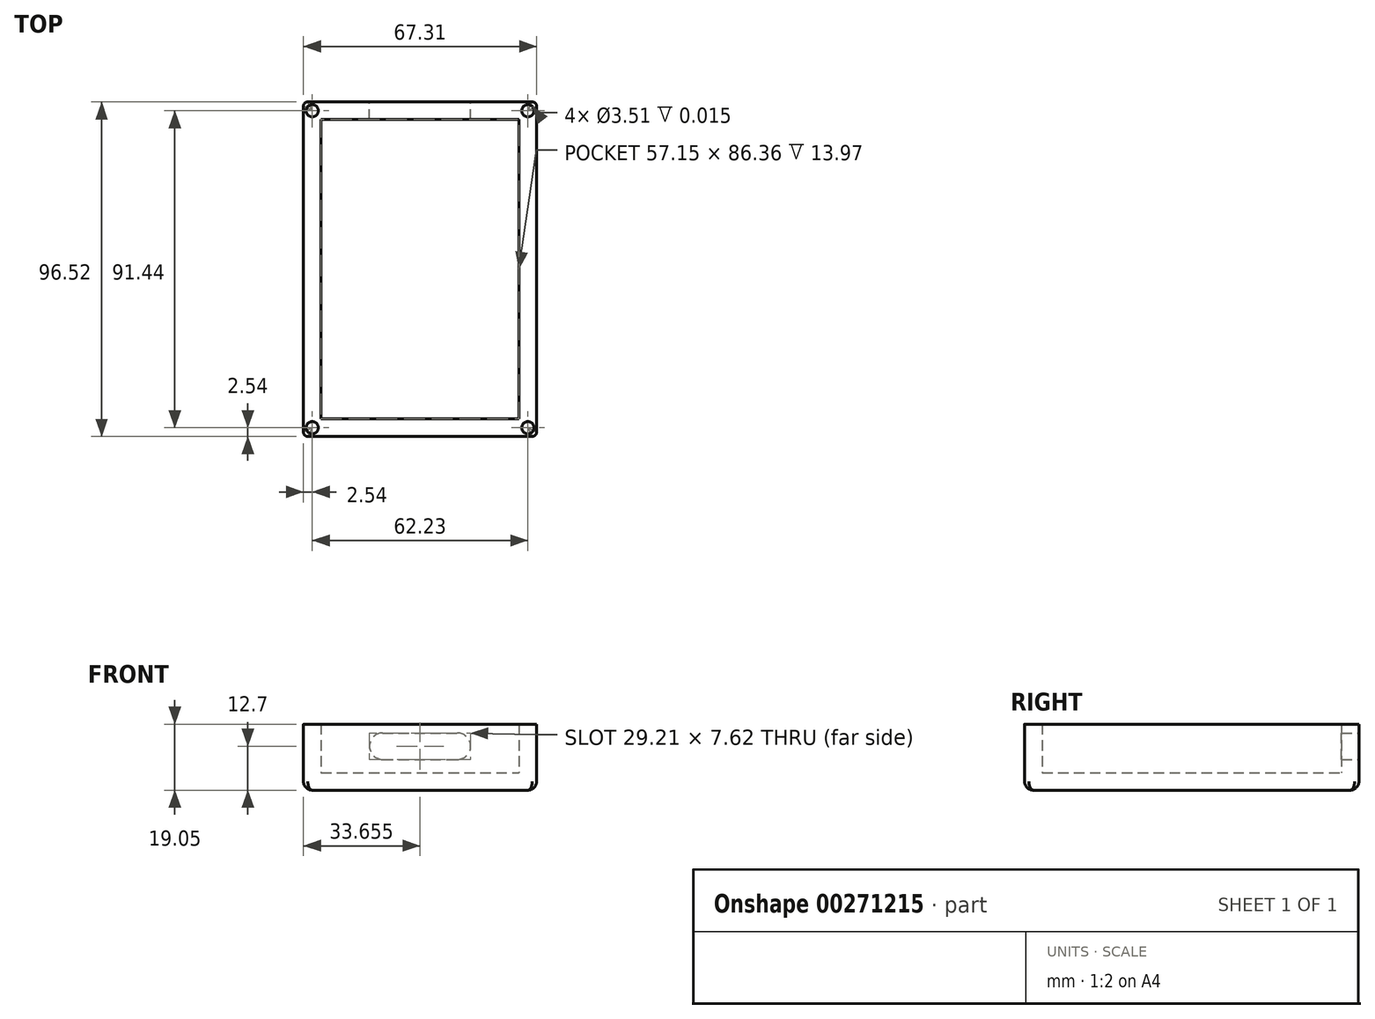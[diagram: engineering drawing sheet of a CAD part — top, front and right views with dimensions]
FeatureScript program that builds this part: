
annotation { "Feature Type Name" : "Feature", "Feature Type Description" : "" }
export const myFeature = defineFeature(function(context is Context, id is Id, definition is map)
    precondition{}
    {
        {
            var Q0;
            Q0=qCreatedBy(makeId("Top.planeOp"),FACE);
            var sketch = newSketch(context, id + "F0", { "sketchPlane" : qUnion([Q0])});
            skLineSegment(sketch, "E0.bottom", {"start": v(1.27, 0) * mm, "end": v(66.04, 0) * mm});
            skLineSegment(sketch, "E0.top", {"start": v(1.27, 96.52) * mm, "end": v(66.04, 96.52) * mm});
            skLineSegment(sketch, "E0.left", {"start": v(0, 1.27) * mm, "end": v(0, 95.25) * mm});
            skLineSegment(sketch, "E0.right", {"start": v(67.31, 1.27) * mm, "end": v(67.3, 95.25) * mm});
            skPoint(sketch, "E1.visualSharp", {"position": v(0, 96.52) * mm});
            skArc(sketch, "E1.filletArc", {"start": v(1.27, 96.52) * mm, "mid": v(0.37, 96.15) * mm, "end": v(0, 95.25) * mm});
            skPoint(sketch, "E2.visualSharp", {"position": v(67.3, 96.52) * mm});
            skArc(sketch, "E2.filletArc", {"start": v(67.31, 95.25) * mm, "mid": v(66.94, 96.15) * mm, "end": v(66.04, 96.52) * mm});
            skPoint(sketch, "E3.visualSharp", {"position": v(67.31, 0) * mm});
            skArc(sketch, "E3.filletArc", {"start": v(66.04, 0) * mm, "mid": v(66.94, 0.37) * mm, "end": v(67.31, 1.27) * mm});
            skPoint(sketch, "E4.visualSharp", {"position": v(0, 0) * mm});
            skArc(sketch, "E4.filletArc", {"start": v(0, 1.27) * mm, "mid": v(0.37, 0.37) * mm, "end": v(1.27, 0) * mm});
            skSolve(sketch);
        }
        {
            var Q0;
            Q0 = qSketchRegion(id + "F0", true);
            extrude(context, id + "F1", {"entities" : qUnion([Q0]), "depth" : 19.05 * mm});
        }
        {
            var Q0;
            Q0=makeQuery(id+"F1.opExtrude","CAP_FACE",FACE,{"disambiguationData":[OSD([sQuery(id+"F0.wireOp",EDGE,"E0.bottom"),sQuery(id+"F0.wireOp",EDGE,"E0.top"),sQuery(id+"F0.wireOp",EDGE,"E0.left"),sQuery(id+"F0.wireOp",EDGE,"E0.right"),sQuery(id+"F0.wireOp",EDGE,"E1.filletArc"),sQuery(id+"F0.wireOp",EDGE,"E2.filletArc"),sQuery(id+"F0.wireOp",EDGE,"E3.filletArc"),sQuery(id+"F0.wireOp",EDGE,"E4.filletArc")])],"isStart":false});
            shell(context, id + "F2", {"entities" : qUnion([Q0]), "thickness" : 5.08 * mm});
        }
        {
            var Q0;
            Q0=makeQuery(id+"F1.opExtrude","SWEPT_FACE",FACE,{"disambiguationData":[OSD([sQuery(id+"F0.wireOp",EDGE,"E0.top")])]});
            var sketch = newSketch(context, id + "F3", { "sketchPlane" : qUnion([Q0])});
            skLineSegment(sketch, "E5", {"start": v(-1.27, 12.7) * mm, "end": v(-22.86, 12.7) * mm, "construction": true});
            skLineSegment(sketch, "E6", {"start": v(-22.86, 12.7) * mm, "end": v(-44.45, 12.7) * mm, "construction": true});
            skLineSegment(sketch, "E7", {"start": v(-44.45, 12.7) * mm, "end": v(-66.04, 12.7) * mm, "construction": true});
            skLineSegment(sketch, "E8.bottom", {"start": v(-22.86, 8.89) * mm, "end": v(-44.45, 8.89) * mm});
            skLineSegment(sketch, "E8.top", {"start": v(-22.86, 16.51) * mm, "end": v(-44.45, 16.51) * mm});
            skLineSegment(sketch, "E8.left", {"start": v(-22.86, 8.89) * mm, "end": v(-22.86, 16.51) * mm, "construction": true});
            skLineSegment(sketch, "E8.right", {"start": v(-44.45, 8.89) * mm, "end": v(-44.45, 16.51) * mm, "construction": true});
            skArc(sketch, "E9", {"start": v(-22.86, 8.89) * mm, "mid": v(-19.05, 12.7) * mm, "end": v(-22.86, 16.5) * mm});
            skArc(sketch, "E10", {"start": v(-44.45, 16.5) * mm, "mid": v(-48.26, 12.7) * mm, "end": v(-44.45, 8.89) * mm});
            skSolve(sketch);
        }
        {
            var Q0;
            Q0 = qSketchRegion(id + "F3", true);
            extrude(context, id + "F4", {"entities" : qUnion([Q0]), "operationType" : NewBodyOperationType.REMOVE, "oppositeDirection" : true, "depth" : 25.4 * mm});
        }
        {
            var Q0;
            Q0=makeQuery(id+"F1.opExtrude","CAP_FACE",FACE,{"disambiguationData":[OSD([sQuery(id+"F0.wireOp",EDGE,"E0.bottom"),sQuery(id+"F0.wireOp",EDGE,"E0.top"),sQuery(id+"F0.wireOp",EDGE,"E0.left"),sQuery(id+"F0.wireOp",EDGE,"E0.right"),sQuery(id+"F0.wireOp",EDGE,"E1.filletArc"),sQuery(id+"F0.wireOp",EDGE,"E2.filletArc"),sQuery(id+"F0.wireOp",EDGE,"E3.filletArc"),sQuery(id+"F0.wireOp",EDGE,"E4.filletArc")])],"isStart":false});
            var sketch = newSketch(context, id + "F5", { "sketchPlane" : qUnion([Q0])});
            skCircle(sketch, "E11", {"center": v(2.54, 93.98) * mm, "radius": 1.75 * mm});
            skLineSegment(sketch, "E12.bottom", {"start": v(2.54, 93.98) * mm, "end": v(64.77, 93.98) * mm, "construction": true});
            skLineSegment(sketch, "E12.top", {"start": v(2.54, 2.54) * mm, "end": v(64.77, 2.54) * mm, "construction": true});
            skLineSegment(sketch, "E12.left", {"start": v(2.54, 93.98) * mm, "end": v(2.54, 2.54) * mm, "construction": true});
            skLineSegment(sketch, "E12.right", {"start": v(64.77, 93.98) * mm, "end": v(64.77, 2.54) * mm, "construction": true});
            skCircle(sketch, "E13", {"center": v(64.77, 93.98) * mm, "radius": 1.75 * mm});
            skCircle(sketch, "E14", {"center": v(2.54, 2.54) * mm, "radius": 1.75 * mm});
            skCircle(sketch, "E15", {"center": v(64.77, 2.54) * mm, "radius": 1.75 * mm});
            skSolve(sketch);
        }
        {
            var Q0;
            Q0 = qSketchRegion(id + "F5", true);
            extrude(context, id + "F6", {"entities" : qUnion([Q0]), "operationType" : NewBodyOperationType.REMOVE, "oppositeDirection" : true, "depth" : 3 / 203.2 * mm});
        }
        {
            var Q0;
            Q0=makeQuery(id+"F1.opExtrude","CAP_EDGE",EDGE,{"disambiguationData":[OSD([sQuery(id+"F0.wireOp",EDGE,"E0.top")])],"isStart":true});
            var Q1;
            Q1=makeQuery(id+"F1.opExtrude","CAP_EDGE",EDGE,{"disambiguationData":[OSD([sQuery(id+"F0.wireOp",EDGE,"E0.left")])],"isStart":true});
            var Q2;
            Q2=makeQuery(id+"F1.opExtrude","CAP_EDGE",EDGE,{"disambiguationData":[OSD([sQuery(id+"F0.wireOp",EDGE,"E0.right")])],"isStart":true});
            var Q3;
            Q3=makeQuery(id+"F1.opExtrude","CAP_EDGE",EDGE,{"disambiguationData":[OSD([sQuery(id+"F0.wireOp",EDGE,"E0.bottom")])],"isStart":true});
            fillet(context, id + "F7", {"entities" : qUnion([Q0, Q1, Q2, Q3]), "radius" : 2.54 * mm, "tangentPropagation" : true, "allowEdgeOverflow" : false});
        }
    });
